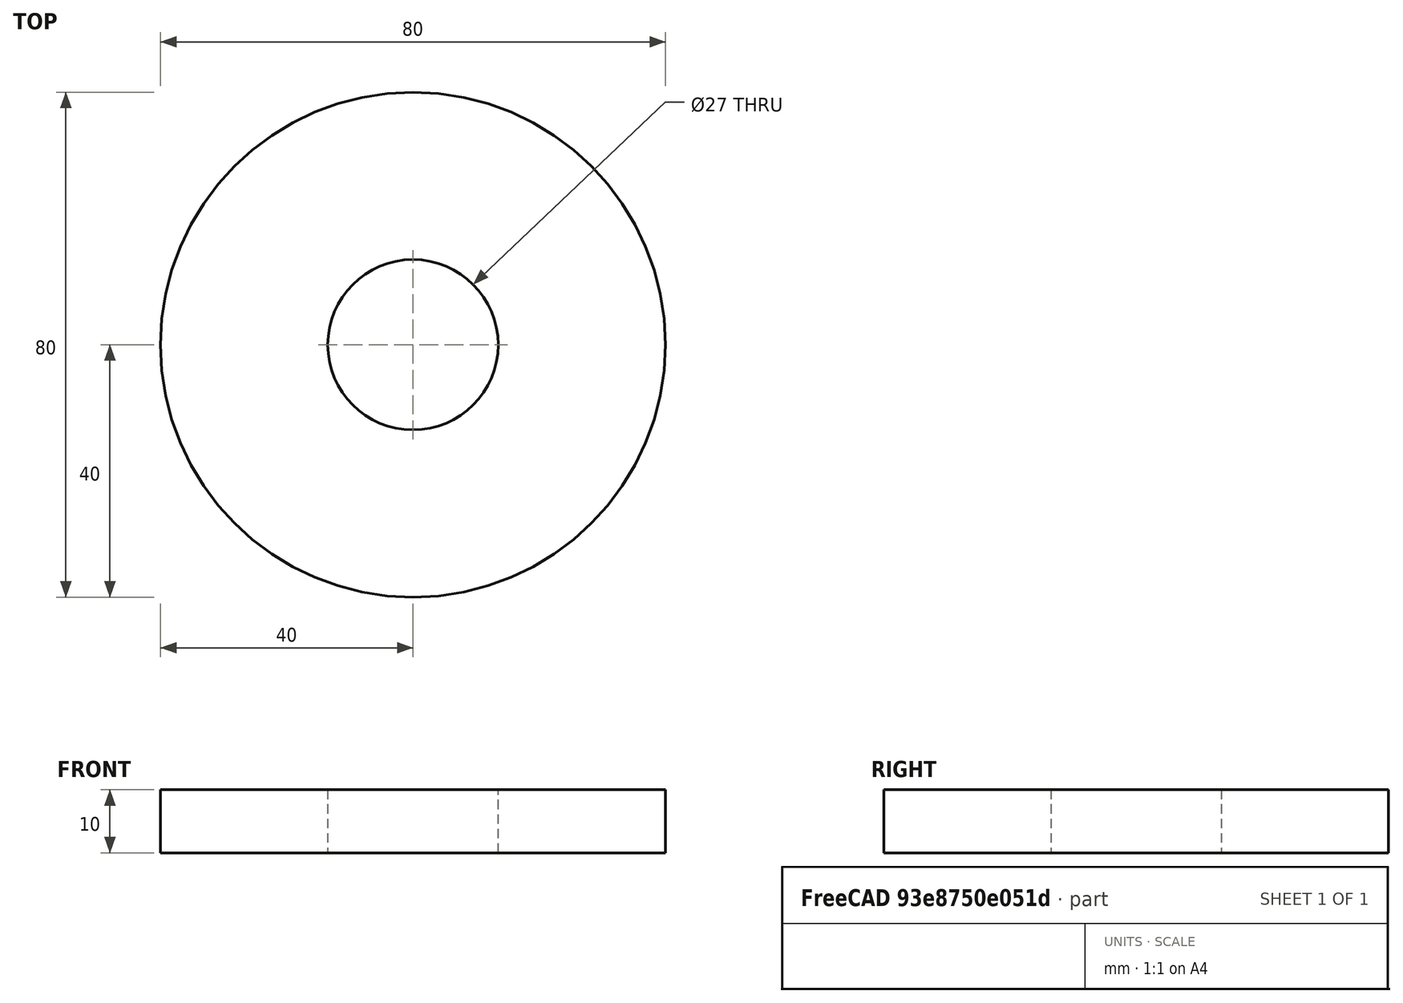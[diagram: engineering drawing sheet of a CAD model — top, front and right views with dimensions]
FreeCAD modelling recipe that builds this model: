
FCSTD DOCUMENT  (FreeCAD 0.19R24276 (Git))
Label: Ring_under_katushka_1_print
License: All rights reserved
LicenseURL: http://en.wikipedia.org/wiki/All_rights_reserved
objects: Sketcher::SketchObject×1, PartDesign::Pad×1, PartDesign::Body×1
note: 4 computed .brp shape members not serialized (recipe doc carries the construction recipe); baked Part::Feature solids carry a one-line shape summary decoded from their .brp

FEATURE [Sketcher::SketchObject] Sketch
  FullyConstrained = true
  MapMode = 5
  Support = -> [XY_Plane]
  sketch-geometry (2):
    g0: Circle CenterX=0 CenterY=0 CenterZ=0 NormalX=0 NormalY=0 NormalZ=1 AngleXU=0 Radius=13.5
    g1: Circle CenterX=0 CenterY=0 CenterZ=0 NormalX=0 NormalY=0 NormalZ=1 AngleXU=0 Radius=40
  constraints (4):
    c: Coincident(g0,g-1)
    c: Coincident(g1,g0)
    c: Diameter(g0) = 27
    c: Diameter(g1) = 80
FEATURE [PartDesign::Pad] Pad
  Direction = (1,1,1)
  Length = 10
  Length2 = 100
  Profile = -> Sketch
  Type = 0
FEATURE [PartDesign::Body] Body
  Group = -> [Sketch,Pad]
  Origin = -> Origin
  Tip = -> Pad
